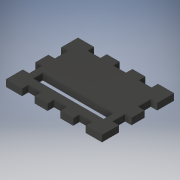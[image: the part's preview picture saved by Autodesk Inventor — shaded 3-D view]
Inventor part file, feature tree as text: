
AUTODESK INVENTOR PART (.ipt)
format: ipt  version: 2019 (Build 230136000, 136)  size: 179,200 bytes
history: native  units: mm
features: extrude x2, sketch x2, projected_geometry x1
ambient origin geometry x8: Origin, YZ Plane, XZ Plane, XY Plane, X Axis, Y Axis, Z Axis, Center Point
bodies: Solid1 (feature_tree)
feature tree (5):
  extrude  "Extrusion1"  Depth=45.0mm
  extrude  "Extrusion2"  Depth=4.0mm
  sketch  "Sketch1"  dims[d0=60.0mm d1=45.0mm]
  sketch  "Sketch2"  dims[d2=4.0mm d3=0.0mm d4=4.0mm d7=8.0mm d8=8.0mm d9=4.0mm d10=8.0mm d11=4.0mm d12=4.0mm d13=0.0mm d14=44.0mm d15=6.0mm d16=8.0mm d17=9.0mm]
  projected_geometry  "Projected Loop1"
